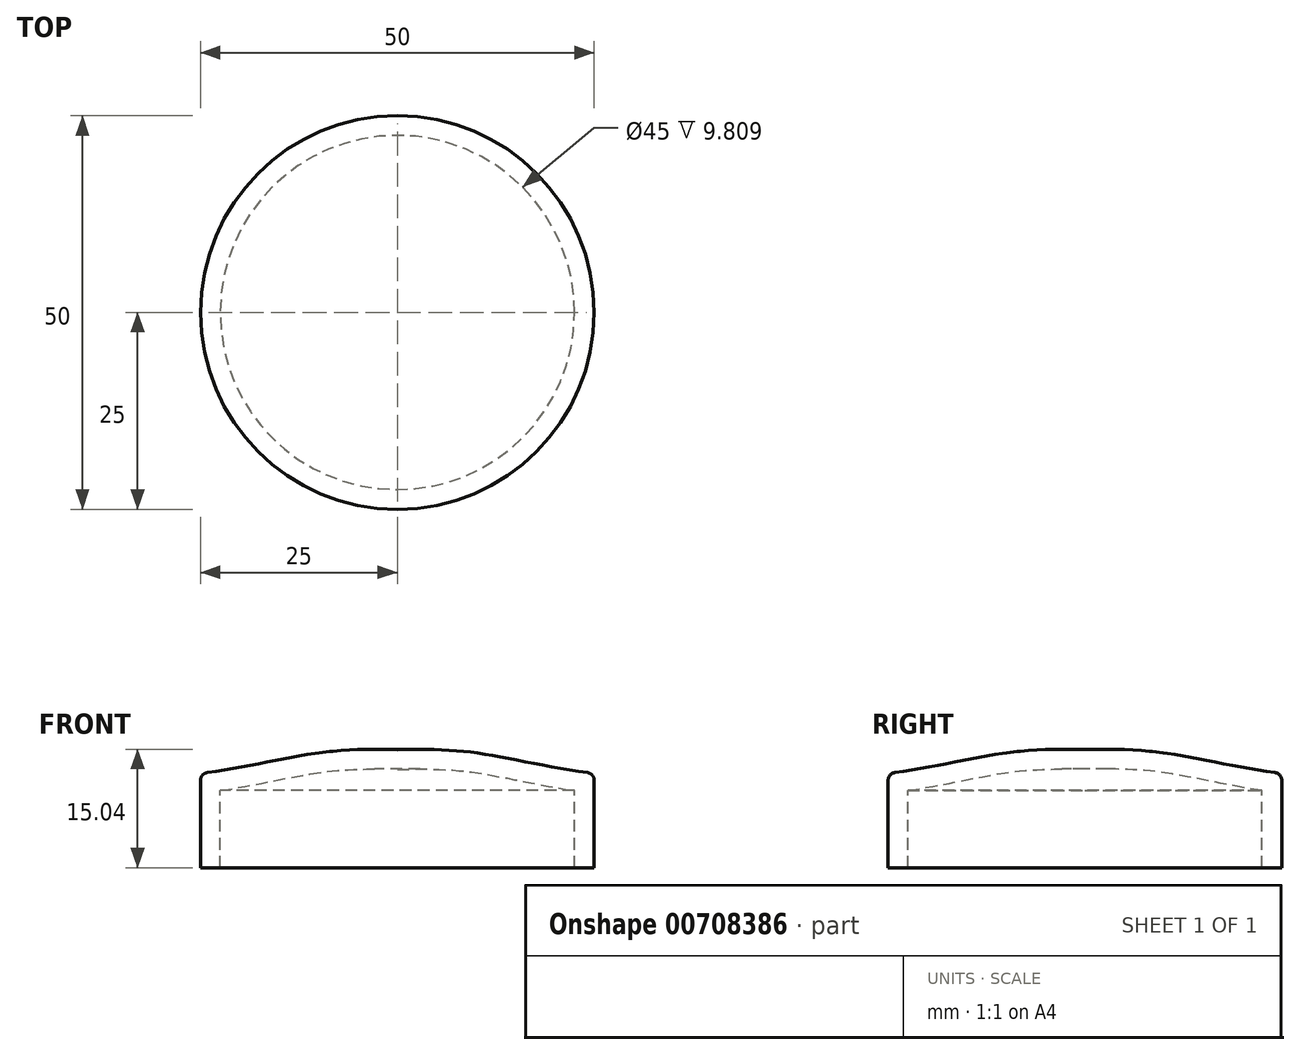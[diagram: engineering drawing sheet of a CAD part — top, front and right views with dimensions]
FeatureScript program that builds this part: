
annotation { "Feature Type Name" : "Feature", "Feature Type Description" : "" }
export const myFeature = defineFeature(function(context is Context, id is Id, definition is map)
    precondition{}
    {
        {
            var Q0;
            Q0=qCreatedBy(makeId("Front.planeOp"),FACE);
            var sketch = newSketch(context, id + "F0", { "sketchPlane" : qUnion([Q0])});
            skLineSegment(sketch, "E0", {"start": v(0, 0) * mm, "end": v(0, -15) * mm});
            skLineSegment(sketch, "E1", {"start": v(0, -15) * mm, "end": v(25, -15) * mm});
            skLineSegment(sketch, "E2", {"start": v(25, -15) * mm, "end": v(25, -3) * mm});
            skFitSpline(sketch, "E3", {"points": [v(0, 0) * mm, v(11.44, -0.62) * mm, v(25, -3) * mm], "startDerivative": vector(31.99, 0.72) * mm, "endDerivative": vector(26.54, -3) * mm});
            skSolve(sketch);
        }
        {
            var Q0;
            Q0 = qSketchRegion(id + "F0", true);
            var Q1;
            Q1=sQuery(id+"F0.wireOp",EDGE,"E0");
            revolve(context, id + "F1", {"surfaceOperationType" : NewSurfaceOperationType.NEW, "entities" : qUnion([Q0]), "axis" : qUnion([Q1]), "revolveType" : RevolveType.FULL});
        }
        {
            var Q0;
            Q0=makeQuery(id+"F1.opRevolve","SWEPT_EDGE",EDGE,{"disambiguationData":[OSD([sQuery(id+"F0.wireOp",EDGE,"E2"),sQuery(id+"F0.wireOp",EDGE,"E3")])]});
            fillet(context, id + "F2", {"entities" : qUnion([Q0]), "radius" : 1 * mm, "tangentPropagation" : true, "allowEdgeOverflow" : false});
        }
        {
            var Q0;
            Q0=makeQuery(id+"F1.opRevolve","SWEPT_FACE",FACE,{"disambiguationData":[OSD([sQuery(id+"F0.wireOp",EDGE,"E1")])]});
            shell(context, id + "F3", {"entities" : qUnion([Q0]), "thickness" : 2.5 * mm});
        }
    });
